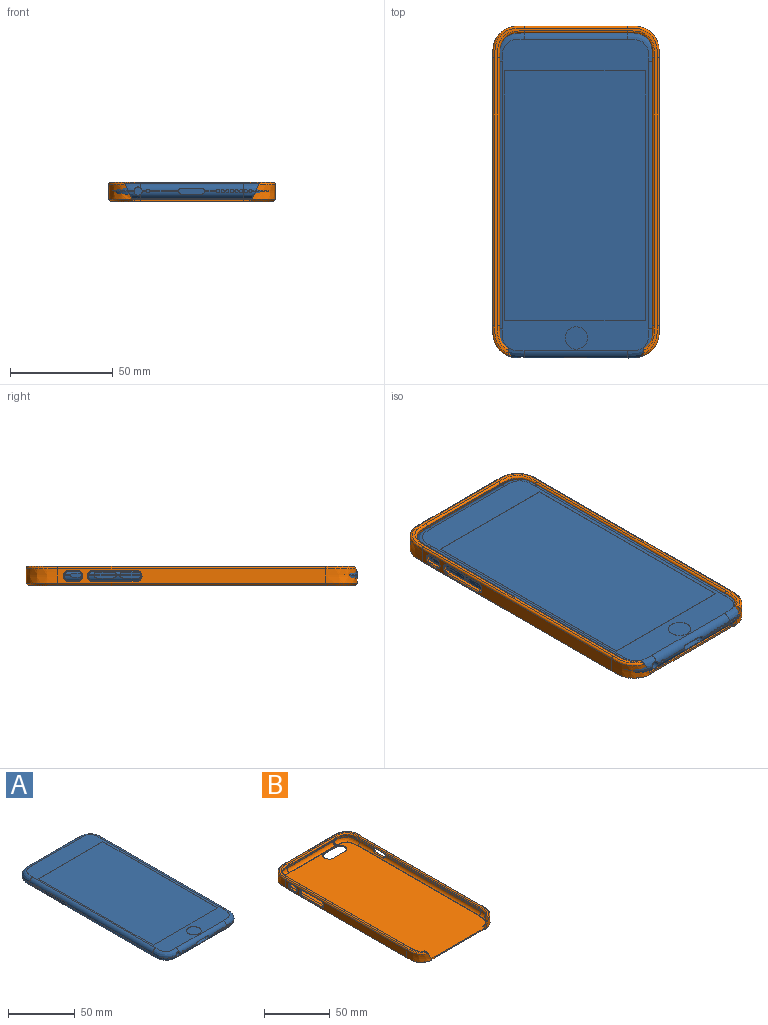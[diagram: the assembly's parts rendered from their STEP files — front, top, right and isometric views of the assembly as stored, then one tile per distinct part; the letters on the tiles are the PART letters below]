
ASSEMBLY  parts=2 mates=1
PART A: 108 faces, bbox 79.2x158.7x8 mm
  f0: plane 4.66x0.2mm, normal (-1,0,0), area 0.9mm2, adj f20,f43,f51,f102
  f1: plane 1.68x0.2mm, normal (-1,0,0), area 0.3mm2, adj f43,f51,f90,f95
  f2: plane 5.7x0.2mm, normal (-1,0,0), area 1.1mm2, adj f43,f51,f88,f104
  f3: plane 103.64x0.2mm, normal (1,0,0), area 20.7mm2, adj f12,f42,f50,f81
  f4: plane 0.66x0.2mm, normal (0,-1,0), area 0.1mm2, adj f46,f54,f72,f74
  f5: plane 0.2x0.15mm, normal (0,-1,0), area 0mm2, adj f16,f46,f54,f72
  f6: plane 5.71x0.2mm, normal (0,-1,0), area 1.1mm2, adj f46,f54,f59,f70
  f7: plane 0.66x0.2mm, normal (0,-1,0), area 0.1mm2, adj f46,f54,f65,f74
  f8: plane 0.66x0.2mm, normal (0,-1,0), area 0.1mm2, adj f46,f54,f63,f65
  f9: plane 0.66x0.2mm, normal (0,-1,0), area 0.1mm2, adj f46,f54,f61,f63
  f10: plane 0.66x0.2mm, normal (0,-1,0), area 0.1mm2, adj f46,f54,f59,f61
  f11: plane 14.01x0.2mm, normal (0,-1,0), area 2.8mm2, adj f46,f54,f57,f68
  f12: extruded ~13.98x9.78mm, area 3.8mm2, adj f3,f44,f52,f78
  f13: extruded ~0.66x0.2mm, area 0.1mm2, adj f44,f52,f76,f78
  f14: plane 151.62x71.34mm, normal (0,0,1), area 2367.4mm2, adj f30,f32,f33,f34,f35,f47,f48,f49
  f15: plane 2.09x0.2mm, normal (0,-1,0), area 0.4mm2, adj f46,f54,f55,f57
  f16: extruded ~0.52x0.2mm, area 0.1mm2, adj f5,f44,f52,f76
  f17: plane 15.88x0.2mm, normal (1,0,0), area 3.2mm2, adj f18,f42,f50,f83
  f18: extruded ~14.13x14.13mm, area 4.7mm2, adj f17,f19,f38,f40,f48
  f19: plane 50.18x0.2mm, normal (0,1,0), area 10mm2, adj f18,f20,f37,f39,f47
  f20: extruded ~14.13x14.13mm, area 4.7mm2, adj f0,f19,f41,f49
  f21: plane 90.97x0.2mm, normal (-1,0,0), area 18.2mm2, adj f22,f43,f51,f97
  f22: extruded ~14.08x11.12mm, area 4.1mm2, adj f21,f45,f53,f55
  f23: plane 151.62x71.34mm, normal (0,0,-1), area 10708mm2, adj f24,f26,f28,f39,f40,f41,f42,f43
  f24: cylinder r=3.83mm len=7.66mm, axis (0,0,1), area 16.1mm2, adj f23,f25,f37,f38
  f25: plane 7.66x7.66mm, normal (0,0,-1), area 46.1mm2, adj f24
  f26: cylinder r=0.8mm len=1.6mm, axis (0,0,-1), area 0.5mm2, adj f23,f27
  f27: plane 1.6x1.6mm, normal (0,0,-1), area 2mm2, adj f26
  f28: cylinder r=2.06mm len=4.11mm, axis (0,0,-1), area 1.3mm2, adj f23,f29
  f29: plane 4.11x4.11mm, normal (0,0,-1), area 13.3mm2, adj f28
  f30: cylinder r=5.45mm len=10.9mm, axis (0,0,1), area 3.4mm2, adj f14,f31
  f31: plane 10.9x10.9mm, normal (0,0,1), area 93.3mm2, adj f30
  f32: plane 68.36x0.1mm, normal (0,-1,0), area 6.8mm2, adj f14,f33,f35,f36
  f33: plane 121.54x0.1mm, normal (1,0,0), area 12.2mm2, adj f14,f32,f34,f36
  f34: plane 68.36x0.1mm, normal (0,1,0), area 6.8mm2, adj f14,f33,f35,f36
  f35: plane 121.54x0.1mm, normal (-1,0,0), area 12.2mm2, adj f14,f32,f34,f36
  f36: plane 121.54x68.36mm, normal (0,0,1), area 8308.5mm2, adj f32,f33,f34,f35
  f37: bspline ~3.66x3.64mm, area 4.8mm2, adj f19,f24,f38,f39
  f38: bspline ~3.61x3.6mm, area 5.3mm2, adj f18,f24,f37,f40
  f39: cylinder r=3.55mm len=49.3mm, axis (-1,0,0), area 274.9mm2, adj f19,f23,f37,f41
  f40: bspline ~16.8x14.8mm, area 114.8mm2, adj f18,f23,f38,f42
  f41: bspline ~16.8x16.8mm, area 120.2mm2, adj f20,f23,f39,f43
  f42: cylinder r=3.55mm len=130.46mm, axis (0,1,0), area 727.5mm2, adj f3,f17,f23,f40,f44,f80
  f43: cylinder r=3.55mm len=130.46mm, axis (0,-1,0), area 727.5mm2, adj f0,f1,f2,f21,f23,f41,f45,f87
  f44: bspline ~16.8x16.8mm, area 118.5mm2, adj f12,f13,f16,f23,f42,f46,f76,f78
  f45: bspline ~16.8x16.8mm, area 117.7mm2, adj f22,f23,f43,f46,f55
  f46: cylinder r=3.55mm len=50.18mm, axis (1,0,0), area 255.6mm2, adj f4,f5,f6,f7,f8,f9,f10,f11
  f47: cylinder r=3.55mm len=50.18mm, axis (1,0,0), area 279.8mm2, adj f14,f19,f48,f49
  f48: bspline ~16.8x16.8mm, area 120.2mm2, adj f14,f18,f47,f50
  f49: bspline ~16.8x14.8mm, area 120.2mm2, adj f14,f20,f47,f51
  f50: cylinder r=3.55mm len=130.46mm, axis (0,-1,0), area 727.5mm2, adj f3,f14,f17,f48,f52,f86
  f51: cylinder r=3.55mm len=130.46mm, axis (0,1,0), area 727.5mm2, adj f0,f1,f2,f14,f21,f49,f53,f93
  f52: bspline ~16.8x16.8mm, area 118.4mm2, adj f12,f13,f14,f16,f50,f54,f76,f78
  f53: bspline ~16.8x16.8mm, area 117.7mm2, adj f14,f22,f51,f54,f55
  f54: cylinder r=3.55mm len=50.18mm, axis (-1,0,0), area 255.6mm2, adj f4,f5,f6,f7,f8,f9,f10,f11
  f55: cylinder r=2.01mm len=4.02mm, axis (0,-1,0), area 34.2mm2, adj f15,f22,f45,f46,f53,f54,f56
  f56: plane 4.02x4.02mm, normal (0,-1,0), area 12.7mm2, adj f55
  f57: cylinder r=0.8mm len=3mm, axis (0,-1,0), area 14.9mm2, adj f11,f15,f46,f54,f58
  f58: plane 1.6x1.6mm, normal (0,-1,0), area 2mm2, adj f57
  f59: cylinder r=0.8mm len=3mm, axis (0,-1,0), area 14.9mm2, adj f6,f10,f46,f54,f60
  f60: plane 1.6x1.6mm, normal (0,-1,0), area 2mm2, adj f59
  f61: cylinder r=0.8mm len=3mm, axis (0,-1,0), area 14.9mm2, adj f9,f10,f46,f54,f62
  f62: plane 1.6x1.6mm, normal (0,-1,0), area 2mm2, adj f61
  f63: cylinder r=0.8mm len=3mm, axis (0,-1,0), area 14.9mm2, adj f8,f9,f46,f54,f64
  f64: plane 1.6x1.6mm, normal (0,-1,0), area 2mm2, adj f63
  f65: cylinder r=0.8mm len=3mm, axis (0,-1,0), area 14.9mm2, adj f7,f8,f46,f54,f66
  f66: plane 1.6x1.6mm, normal (0,-1,0), area 2mm2, adj f65
  f67: plane 9.84x2.72mm, normal (0,0,-1), area 26.8mm2, adj f54,f68,f70,f71
  f68: cylinder r=1.47mm len=3mm, axis (0,-1,0), area 13.3mm2, adj f11,f46,f54,f67,f69,f71
  f69: plane 9.84x2.72mm, normal (0,0,1), area 26.8mm2, adj f46,f68,f70,f71
  f70: cylinder r=1.47mm len=3mm, axis (0,-1,0), area 13.3mm2, adj f6,f46,f54,f67,f69,f71
  f71: plane 12.79x2.95mm, normal (0,-1,0), area 35.9mm2, adj f67,f68,f69,f70
  f72: cylinder r=0.8mm len=3mm, axis (0,-1,0), area 15.1mm2, adj f4,f5,f46,f54,f73
  f73: plane 1.6x1.6mm, normal (0,-1,0), area 2mm2, adj f72
  f74: cylinder r=0.8mm len=3mm, axis (0,-1,0), area 15.1mm2, adj f4,f7,f46,f54,f75
  f75: plane 1.6x1.6mm, normal (0,-1,0), area 2mm2, adj f74
  f76: cylinder r=0.8mm len=3mm, axis (0,-1,0), area 14.9mm2, adj f13,f16,f44,f52,f77
  f77: plane 1.6x1.6mm, normal (0,-1,0), area 2mm2, adj f76
  f78: cylinder r=0.8mm len=2.96mm, axis (0,-1,0), area 14.6mm2, adj f12,f13,f44,f52,f79
  f79: plane 1.6x1.6mm, normal (0,-1,0), area 2mm2, adj f78
  f80: plane 10.93x1.3mm, normal (-1,0,0), area 13.4mm2, adj f42,f81,f82,f83
  f81: cylinder r=1.4mm len=2.8mm, axis (-1,0,0), area 1.3mm2, adj f3,f80,f82,f84,f85,f86
  f82: plane 8.14x0.3mm, normal (0,0,-1), area 2.4mm2, adj f80,f81,f83,f85
  f83: cylinder r=1.4mm len=2.8mm, axis (-1,0,0), area 1.3mm2, adj f17,f80,f82,f84,f85,f86
  f84: plane 8.14x0.3mm, normal (0,0,1), area 2.4mm2, adj f81,f83,f85,f86
  f85: plane 10.94x2.8mm, normal (1,0,0), area 28.9mm2, adj f81,f82,f83,f84
  f86: plane 10.93x1.3mm, normal (-1,0,0), area 13.4mm2, adj f50,f81,f83,f84
  f87: plane 10.94x1.32mm, normal (1,0,0), area 13.6mm2, adj f43,f88,f89,f90
  f88: cylinder r=1.4mm len=2.8mm, axis (1,0,0), area 1.3mm2, adj f2,f87,f89,f91,f92,f93
  f89: plane 8.14x0.3mm, normal (0,0,-1), area 2.4mm2, adj f87,f88,f90,f92
  f90: cylinder r=1.4mm len=2.8mm, axis (1,0,0), area 1.3mm2, adj f1,f87,f89,f91,f92,f93
  f91: plane 8.14x0.3mm, normal (0,0,1), area 2.4mm2, adj f88,f90,f92,f93
  f92: plane 10.94x2.8mm, normal (-1,0,0), area 28.9mm2, adj f88,f89,f90,f91
  f93: plane 10.93x1.28mm, normal (1,0,0), area 13.2mm2, adj f51,f88,f90,f91
  f94: plane 10.94x1.32mm, normal (1,0,0), area 13.6mm2, adj f43,f95,f96,f97
  f95: cylinder r=1.4mm len=2.8mm, axis (1,0,0), area 1.3mm2, adj f1,f94,f96,f98,f99,f100
  f96: plane 8.14x0.3mm, normal (0,0,-1), area 2.4mm2, adj f94,f95,f97,f99
  f97: cylinder r=1.4mm len=2.8mm, axis (1,0,0), area 1.3mm2, adj f21,f94,f96,f98,f99,f100
  f98: plane 8.14x0.3mm, normal (0,0,1), area 2.4mm2, adj f95,f97,f99,f100
  f99: plane 10.94x2.8mm, normal (-1,0,0), area 28.9mm2, adj f95,f96,f97,f98
  f100: plane 10.93x1.28mm, normal (1,0,0), area 13.2mm2, adj f51,f95,f97,f98
  f101: plane 5.6x0.89mm, normal (1,0,0), area 4.6mm2, adj f43,f102,f103,f104
  f102: cylinder r=0.98mm len=1.97mm, axis (1,0,0), area 1.3mm2, adj f0,f101,f103,f105,f106,f107
  f103: plane 3.64x0.43mm, normal (0,0,-1), area 1.6mm2, adj f101,f102,f104,f106
  f104: cylinder r=0.98mm len=1.97mm, axis (1,0,0), area 1.3mm2, adj f2,f101,f103,f105,f106,f107
  f105: plane 3.64x0.43mm, normal (0,0,1), area 1.6mm2, adj f102,f104,f106,f107
  f106: plane 5.61x1.97mm, normal (-1,0,0), area 10.2mm2, adj f102,f103,f104,f105
  f107: plane 5.6x0.88mm, normal (1,0,0), area 4.5mm2, adj f51,f102,f104,f105
PART B: 108 faces, bbox 81.6x161.8x9.7 mm
  f0: extruded ~15.39x11.51mm, area 145.7mm2, adj f23,f66,f82,f89
  f1: plane 159.64x79.46mm, normal (0,0,-1), area 12304.5mm2, adj f27,f28,f29,f30,f68,f69,f70,f71
  f2: extruded ~12.01x8.14mm, area 5.8mm2, adj f6,f13,f26,f67
  f3: extruded ~15.39x11.51mm, area 145.7mm2, adj f24,f67,f85,f95
  f4: extruded ~11.19x4.91mm, area 4.6mm2, adj f7,f19,f67,f81
  f5: extruded ~13.79x8.49mm, area 3.6mm2, adj f6,f7,f39,f67
  f6: bspline ~16.7x10.56mm, area 69.8mm2, adj f2,f5,f50,f67
  f7: bspline ~16.52x9.41mm, area 62.5mm2, adj f4,f5,f53,f67
  f8: extruded ~12.01x8.14mm, area 5.8mm2, adj f9,f26,f35,f66
  f9: plane 130.46x0.36mm, normal (1,0,0), area 46.5mm2, adj f8,f10,f26,f34
  f10: extruded ~12.13x12.13mm, area 7.3mm2, adj f9,f11,f26,f49
  f11: plane 50.22x0.4mm, normal (0,-1,0), area 17.9mm2, adj f10,f12,f26,f46,f47,f48
  f12: extruded ~12.13x12.13mm, area 7.3mm2, adj f11,f13,f26,f36,f47
  f13: plane 130.46x0.36mm, normal (-1,0,0), area 46.5mm2, adj f2,f12,f26,f50
  f14: extruded ~11.19x4.91mm, area 4.6mm2, adj f15,f31,f66,f75
  f15: plane 130.46x0.36mm, normal (1,0,0), area 46.5mm2, adj f14,f16,f32,f76
  f16: extruded ~12.13x12.13mm, area 7.3mm2, adj f15,f17,f52,f77
  f17: plane 50.18x0.36mm, normal (0,-1,0), area 17.9mm2, adj f16,f18,f51,f78
  f18: extruded ~12.13x12.13mm, area 7.3mm2, adj f17,f19,f33,f79
  f19: plane 130.46x0.36mm, normal (-1,0,0), area 46.5mm2, adj f4,f18,f53,f80
  f20: extruded ~15.57x15.5mm, area 189mm2, adj f21,f24,f88,f93
  f21: plane 50.19x7.31mm, normal (0,1,0), area 366.3mm2, adj f20,f22,f86,f92
  f22: extruded ~15.57x15.5mm, area 189mm2, adj f21,f23,f84,f91
  f23: plane 130.46x7.3mm, normal (-1,0,0), area 758.1mm2, adj f0,f22,f83,f90,f96,f97,f98,f99
  f24: plane 130.46x7.3mm, normal (1,0,0), area 878.7mm2, adj f3,f20,f87,f94,f104,f105,f106,f107
  f25: plane 158.46x79.18mm, normal (0,0,1), area 530.1mm2, adj f66,f67,f75,f76,f77,f78,f79,f80
  f26: plane 157.67x74.44mm, normal (0,0,1), area 11374mm2, adj f2,f8,f9,f10,f11,f12,f13,f27
  f27: cylinder r=4.85mm len=9.71mm, axis (0,0,1), area 15.3mm2, adj f1,f26,f28,f30
  f28: plane 12.06x1mm, normal (0,1,0), area 12.1mm2, adj f1,f26,f27,f29
  f29: cylinder r=4.85mm len=9.71mm, axis (0,0,1), area 15.3mm2, adj f1,f26,f28,f30
  f30: plane 12.06x1mm, normal (0,-1,0), area 12.1mm2, adj f1,f26,f27,f29
  f31: bspline ~16.53x9.44mm, area 62.5mm2, adj f14,f32,f45,f66
  f32: cylinder r=3.55mm len=130.46mm, axis (0,1,0), area 445.8mm2, adj f15,f31,f37,f38,f44,f52,f54,f56
  f33: bspline ~16.8x16.8mm, area 89.3mm2, adj f18,f41,f51,f53
  f34: cylinder r=3.55mm len=130.46mm, axis (0,-1,0), area 444.5mm2, adj f9,f35,f37,f38,f44,f49,f55,f56
  f35: bspline ~16.69x10.51mm, area 69.8mm2, adj f8,f34,f45,f66
  f36: bspline ~16.8x14.8mm, area 85.5mm2, adj f12,f41,f47,f50
  f37: plane 3.24x0.2mm, normal (1,0,0), area 0.6mm2, adj f32,f34,f43,f60
  f38: plane 3.28x0.2mm, normal (1,0,0), area 0.7mm2, adj f32,f34,f56,f61
  f39: plane 102.64x0.2mm, normal (-1,0,0), area 20.5mm2, adj f5,f50,f53,f63
  f40: plane 14.88x0.2mm, normal (-1,0,0), area 3mm2, adj f41,f50,f53,f65
  f41: extruded ~14.13x14.13mm, area 4.7mm2, adj f33,f36,f40,f42,f47
  f42: plane 50.18x0.2mm, normal (0,-1,0), area 10mm2, adj f41,f43,f46,f48,f51
  f43: extruded ~14.13x14.13mm, area 4.7mm2, adj f37,f42,f49,f52
  f44: plane 89.96x0.2mm, normal (1,0,0), area 18mm2, adj f32,f34,f45,f57
  f45: extruded ~13.79x8.49mm, area 3.6mm2, adj f31,f35,f44,f66
  f46: bspline ~3.66x3.64mm, area 3.5mm2, adj f11,f42,f47,f48
  f47: bspline ~3.61x3.6mm, area 3.8mm2, adj f11,f12,f36,f41,f46
  f48: cylinder r=3.55mm len=49.3mm, axis (-1,0,0), area 195.8mm2, adj f11,f42,f46,f49
  f49: bspline ~16.8x16.8mm, area 89.3mm2, adj f10,f34,f43,f48
  f50: cylinder r=3.55mm len=130.46mm, axis (0,1,0), area 491.9mm2, adj f6,f13,f36,f39,f40,f62,f63,f65
  f51: cylinder r=3.55mm len=50.18mm, axis (1,0,0), area 199.3mm2, adj f17,f33,f42,f52
  f52: bspline ~16.8x14.8mm, area 89.3mm2, adj f16,f32,f43,f51
  f53: cylinder r=3.55mm len=130.46mm, axis (0,-1,0), area 491.9mm2, adj f7,f19,f33,f39,f40,f63,f64,f65
  f54: plane 20.75x1.7mm, normal (0,0,-1), area 35.2mm2, adj f32,f56,f57,f96
  f55: plane 20.75x1.73mm, normal (0,0,1), area 35.9mm2, adj f34,f56,f57,f99
  f56: cylinder r=2.4mm len=4.8mm, axis (-1,0,0), area 9.6mm2, adj f32,f34,f38,f54,f55,f97
  f57: cylinder r=2.4mm len=4.8mm, axis (-1,0,0), area 9.6mm2, adj f32,f34,f44,f54,f55,f98
  f58: plane 3.64x1.71mm, normal (0,0,-1), area 6.2mm2, adj f32,f60,f61,f100
  f59: plane 3.64x1.72mm, normal (0,0,1), area 6.3mm2, adj f34,f60,f61,f103
  f60: cylinder r=2.4mm len=4.8mm, axis (-1,0,0), area 9.6mm2, adj f32,f34,f37,f58,f59,f101
  f61: cylinder r=2.4mm len=4.8mm, axis (-1,0,0), area 9.6mm2, adj f32,f34,f38,f58,f59,f102
  f62: plane 8.14x1.71mm, normal (0,0,1), area 14mm2, adj f50,f63,f65,f105
  f63: cylinder r=2.4mm len=4.8mm, axis (1,0,0), area 9.6mm2, adj f39,f50,f53,f62,f64,f104
  f64: plane 8.14x1.71mm, normal (0,0,-1), area 14mm2, adj f53,f63,f65,f106
  f65: cylinder r=2.4mm len=4.8mm, axis (1,0,0), area 9.6mm2, adj f40,f50,f53,f62,f64,f107
  f66: plane 8.72x4.72mm, normal (0.91,0,0.42), area 20.6mm2, adj f0,f8,f14,f25,f26,f31,f35,f45
  f67: plane 8.72x4.72mm, normal (-0.91,0,0.42), area 20.6mm2, adj f2,f3,f4,f5,f6,f7,f25,f26
  f68: extruded ~2.94x1mm, area 2.9mm2, adj f1,f26,f69,f74
  f69: plane 50.18x1mm, normal (0,-1,0), area 50.2mm2, adj f1,f26,f68,f70
  f70: extruded ~2.94x1mm, area 2.9mm2, adj f1,f26,f69,f71
  f71: cylinder r=1mm len=1.05mm, axis (0,0,1), area 1.4mm2, adj f1,f26,f70,f72,f89
  f72: plane 0.31x0.31mm, normal (1,0,0), area 0mm2, adj f66,f71,f89
  f73: plane 0.31x0.31mm, normal (-1,0,0), area 0mm2, adj f67,f74,f95
  f74: cylinder r=1mm len=1.05mm, axis (0,0,1), area 1.4mm2, adj f1,f26,f68,f73,f95
  f75: bspline ~14.76x6.42mm, area 20.9mm2, adj f14,f25,f66,f76
  f76: cylinder r=1mm len=130.46mm, axis (0,-1,0), area 204.9mm2, adj f15,f25,f75,f77
  f77: bspline ~15.06x15.06mm, area 33mm2, adj f16,f25,f76,f78
  f78: cylinder r=1mm len=50.18mm, axis (-1,0,0), area 78.8mm2, adj f17,f25,f77,f79
  f79: bspline ~15.06x15.06mm, area 33mm2, adj f18,f25,f78,f80
  f80: cylinder r=1mm len=130.46mm, axis (0,1,0), area 204.9mm2, adj f19,f25,f79,f81
  f81: bspline ~14.76x6.42mm, area 20.9mm2, adj f4,f25,f67,f80
  f82: bspline ~16.91x9.15mm, area 27.3mm2, adj f0,f25,f66,f83
  f83: cylinder r=1mm len=130.46mm, axis (0,1,0), area 204.9mm2, adj f23,f25,f82,f84
  f84: bspline ~17.43x17.04mm, area 39.5mm2, adj f22,f25,f83,f86
  f85: bspline ~16.91x9.15mm, area 27.3mm2, adj f3,f25,f67,f87
  f86: cylinder r=1mm len=50.18mm, axis (1,0,0), area 78.8mm2, adj f21,f25,f84,f88
  f87: cylinder r=1mm len=130.46mm, axis (0,-1,0), area 204.9mm2, adj f24,f25,f85,f88
  f88: bspline ~17.43x17.04mm, area 39.5mm2, adj f20,f25,f86,f87
  f89: bspline ~15.46x12.81mm, area 29.8mm2, adj f0,f1,f71,f72,f90
  f90: plane 130.46x1mm, normal (-0.71,0,-0.71), area 184.5mm2, adj f1,f23,f89,f91
  f91: bspline ~15.5x15.5mm, area 35.3mm2, adj f1,f22,f90,f92
  f92: plane 50.18x1mm, normal (0,0.71,-0.71), area 71mm2, adj f1,f21,f91,f93
  f93: bspline ~15.5x15.5mm, area 35.3mm2, adj f1,f20,f92,f94
  f94: plane 130.46x1mm, normal (0.71,0,-0.71), area 184.5mm2, adj f1,f24,f93,f95
  f95: bspline ~15.46x12.81mm, area 29.8mm2, adj f1,f3,f73,f74,f94
  f96: plane 20.75x0.5mm, normal (-0.71,0,-0.71), area 14.7mm2, adj f23,f54,f97,f98
  f97: cone r=2.4mm half-angle=45deg, axis (-1,0,0), area 5.9mm2, adj f23,f56,f96,f99
  f98: cone r=2.4mm half-angle=45deg, axis (-1,0,0), area 5.9mm2, adj f23,f57,f96,f99
  f99: plane 20.75x0.5mm, normal (-0.71,0,0.71), area 14.7mm2, adj f23,f55,f97,f98
  f100: plane 3.64x0.5mm, normal (-0.71,0,-0.71), area 2.6mm2, adj f23,f58,f101,f102
  f101: cone r=2.4mm half-angle=45deg, axis (-1,0,0), area 5.9mm2, adj f23,f60,f100,f103
  f102: cone r=2.4mm half-angle=45deg, axis (-1,0,0), area 5.9mm2, adj f23,f61,f100,f103
  f103: plane 3.64x0.5mm, normal (-0.71,0,0.71), area 2.6mm2, adj f23,f59,f101,f102
  f104: cone r=2.4mm half-angle=45deg, axis (1,0,0), area 5.9mm2, adj f24,f63,f105,f106
  f105: plane 8.14x0.5mm, normal (0.71,0,0.71), area 5.8mm2, adj f24,f62,f104,f107
  f106: plane 8.14x0.5mm, normal (0.71,0,-0.71), area 5.8mm2, adj f24,f64,f104,f107
  f107: cone r=2.4mm half-angle=45deg, axis (1,0,0), area 5.9mm2, adj f24,f65,f105,f106
PLACE A t=(-4.92,6.69,-4.35)mm
PLACE B t=(-4.73,8.29,-4.8)mm fixed
MATE slider B.f26 <-> A.f23  axis (0,0,1) through (-5.05,6.27,-4.8)mm
